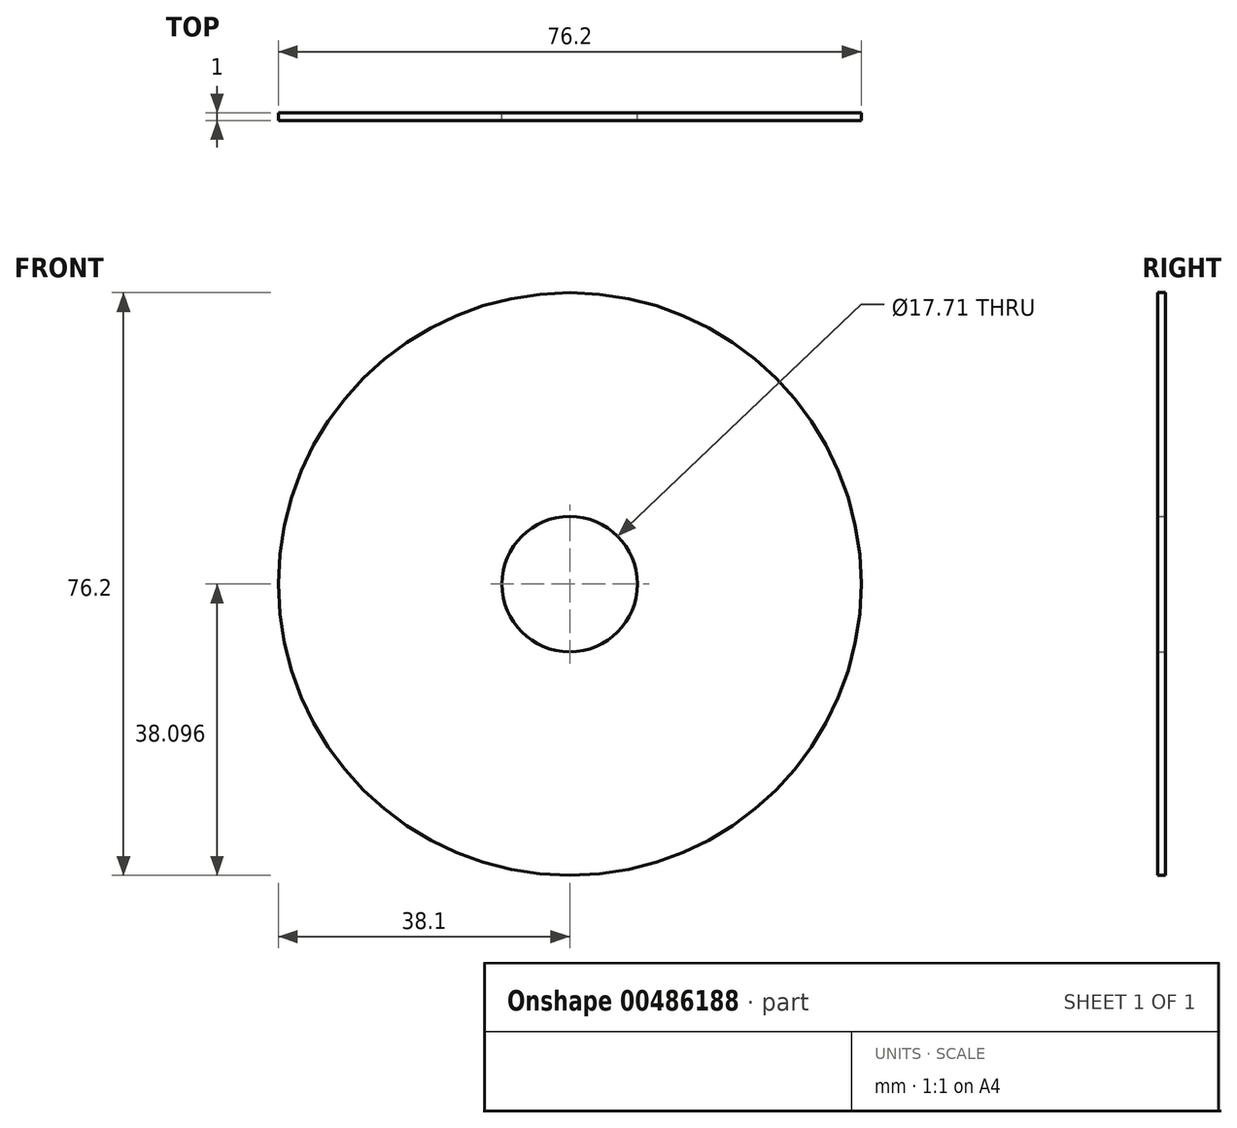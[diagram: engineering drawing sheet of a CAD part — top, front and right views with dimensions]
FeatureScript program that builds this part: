
annotation { "Feature Type Name" : "Feature", "Feature Type Description" : "" }
export const myFeature = defineFeature(function(context is Context, id is Id, definition is map)
    precondition{}
    {
        {
            var Q0;
            Q0=qCreatedBy(makeId("Front.planeOp"),FACE);
            var sketch = newSketch(context, id + "F0", { "sketchPlane" : qUnion([Q0])});
            skCircle(sketch, "E0", {"center": v(-7.19, 7) * mm, "radius": 38.1 * mm});
            skSolve(sketch);
        }
        {
            var Q0;
            Q0=makeQuery(id+"F0.imprint","IMPRINT",FACE,{"disambiguationData":[TD([[makeQuery(id+"F0.imprint","IMPRINT",EDGE,{"derivedFrom":sQuery(id+"F0.wireOp",EDGE,"E0")}),1.0]])]});
            extrude(context, id + "F1", {"entities" : qUnion([Q0]), "depth" : 1 * mm});
        }
        {
            var Q0;
            Q0=makeQuery(id+"F1.opExtrude","CAP_FACE",FACE,{"disambiguationData":[OSD([sQuery(id+"F0.wireOp",EDGE,"E0")])],"isStart":false});
            var sketch = newSketch(context, id + "F2", { "sketchPlane" : qUnion([Q0])});
            skCircle(sketch, "E1", {"center": v(-7.19, 7) * mm, "radius": 3.5 * mm});
            skSolve(sketch);
        }
        {
            var Q0;
            Q0=makeQuery(id+"F2.imprint","IMPRINT",FACE,{"disambiguationData":[TD([[makeQuery(id+"F2.imprint","IMPRINT",EDGE,{"derivedFrom":sQuery(id+"F2.wireOp",EDGE,"E1")}),1.0]])]});
            extrude(context, id + "F3", {"entities" : qUnion([Q0]), "operationType" : NewBodyOperationType.ADD, "depth" : 4 * mm});
        }
        {
            var Q0;
            Q0=makeQuery(id+"F1.opExtrude","CAP_FACE",FACE,{"disambiguationData":[OSD([sQuery(id+"F0.wireOp",EDGE,"E0")])],"isStart":true});
            var sketch = newSketch(context, id + "F4", { "sketchPlane" : qUnion([Q0])});
            skCircle(sketch, "E2", {"center": v(7.19, 7) * mm, "radius": 3.5 * mm});
            skSolve(sketch);
        }
        {
            var Q0;
            Q0=sQuery(id+"F4.wireOp",EDGE,"E2");
            extrude(context, id + "F5", {"bodyType" : ToolBodyType.SURFACE, "surfaceEntities" : qUnion([Q0]), "depth" : 4 * mm});
        }
        {
            var Q0;
            Q0=makeQuery(id+"F1.opExtrude","CAP_FACE",FACE,{"disambiguationData":[OSD([sQuery(id+"F0.wireOp",EDGE,"E0")])],"isStart":true});
            var sketch = newSketch(context, id + "F6", { "sketchPlane" : qUnion([Q0])});
            skCircle(sketch, "E3", {"center": v(7.19, 7) * mm, "radius": 8.86 * mm});
            skSolve(sketch);
        }
        {
            var Q0;
            Q0 = qSketchRegion(id + "F6", true);
            extrude(context, id + "F7", {"entities" : qUnion([Q0]), "operationType" : NewBodyOperationType.REMOVE, "endBound" : BoundingType.THROUGH_ALL, "oppositeDirection" : true, "depth" : 25.4 * mm});
        }
    });
